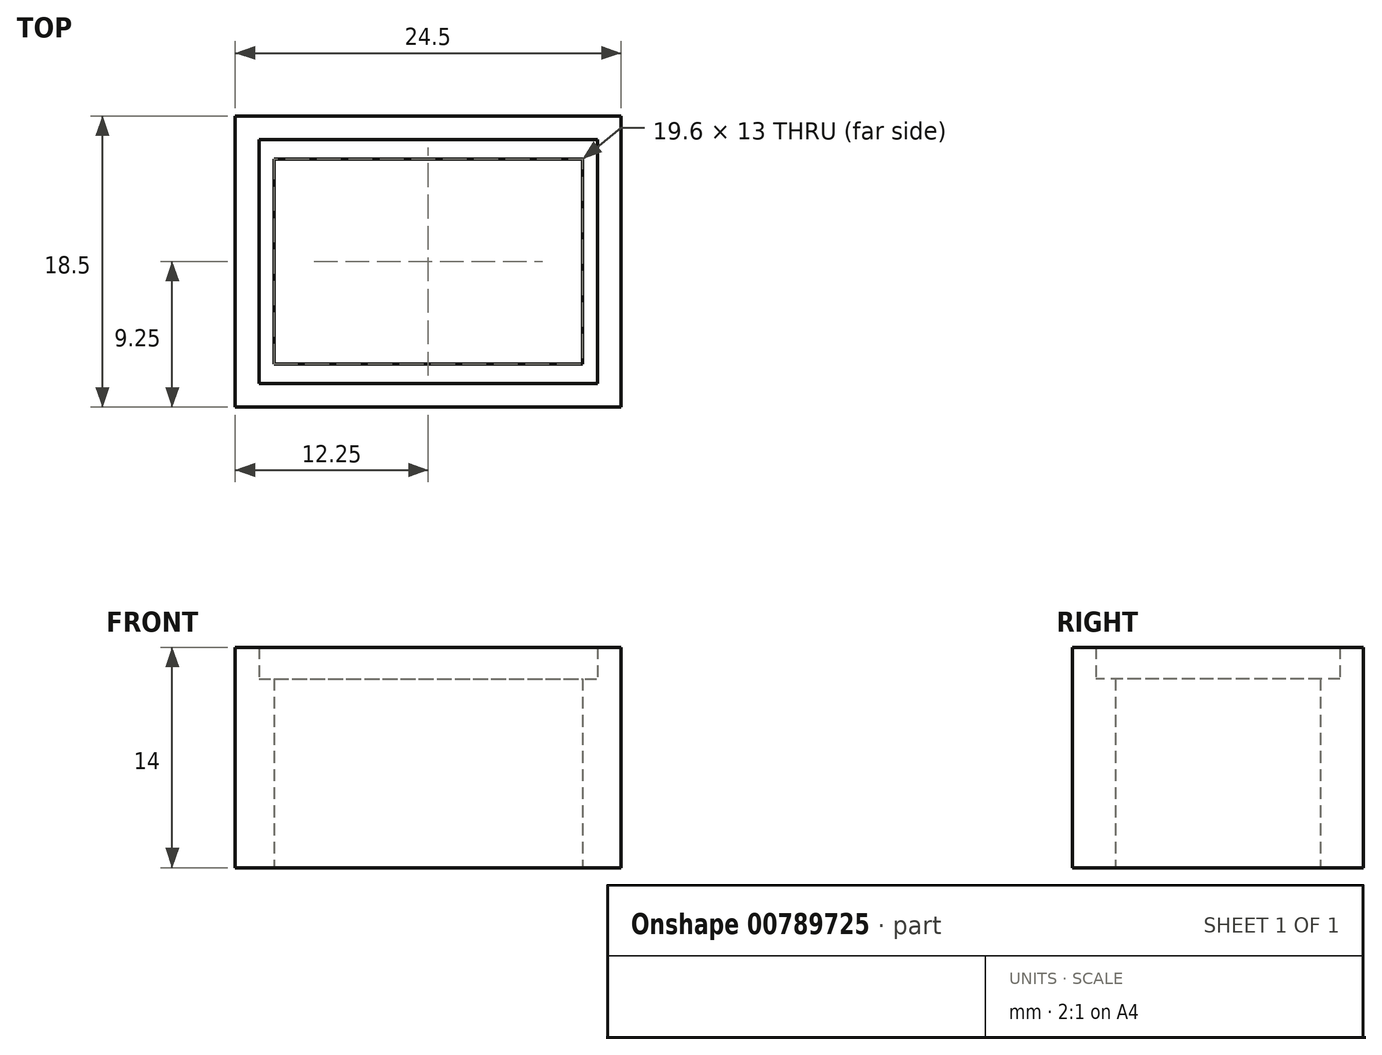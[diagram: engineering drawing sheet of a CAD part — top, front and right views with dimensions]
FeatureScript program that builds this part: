
annotation { "Feature Type Name" : "Feature", "Feature Type Description" : "" }
export const myFeature = defineFeature(function(context is Context, id is Id, definition is map)
    precondition{}
    {
        {
            var Q0;
            Q0=qCreatedBy(makeId("Top.planeOp"),FACE);
            var sketch = newSketch(context, id + "F0", { "sketchPlane" : qUnion([Q0])});
            skLineSegment(sketch, "E0.bottom", {"start": v(-9.8, 6.5) * mm, "end": v(9.8, 6.5) * mm});
            skLineSegment(sketch, "E0.top", {"start": v(-9.8, -6.5) * mm, "end": v(9.8, -6.5) * mm});
            skLineSegment(sketch, "E0.left", {"start": v(-9.8, 6.5) * mm, "end": v(-9.8, -6.5) * mm});
            skLineSegment(sketch, "E0.right", {"start": v(9.8, 6.5) * mm, "end": v(9.8, -6.5) * mm});
            skLineSegment(sketch, "E1.bottom", {"start": v(-10.75, 7.75) * mm, "end": v(10.75, 7.75) * mm});
            skLineSegment(sketch, "E1.top", {"start": v(-10.75, -7.75) * mm, "end": v(10.75, -7.75) * mm});
            skLineSegment(sketch, "E1.left", {"start": v(-10.75, 7.75) * mm, "end": v(-10.75, -7.75) * mm});
            skLineSegment(sketch, "E1.right", {"start": v(10.75, 7.75) * mm, "end": v(10.75, -7.75) * mm});
            skLineSegment(sketch, "E2.bottom", {"start": v(12.25, 9.25) * mm, "end": v(-12.25, 9.25) * mm});
            skLineSegment(sketch, "E2.top", {"start": v(12.25, -9.25) * mm, "end": v(-12.25, -9.25) * mm});
            skLineSegment(sketch, "E2.left", {"start": v(12.25, 9.25) * mm, "end": v(12.25, -9.25) * mm});
            skLineSegment(sketch, "E2.right", {"start": v(-12.25, 9.25) * mm, "end": v(-12.25, -9.25) * mm});
            skPoint(sketch, "E2.middle", {"position": v(0, 0) * mm});
            skSolve(sketch);
        }
        {
            var Q0;
            Q0=makeQuery(id+"F0.imprint","IMPRINT",FACE,{"disambiguationData":[TD([[makeQuery(id+"F0.imprint","IMPRINT",EDGE,{"derivedFrom":sQuery(id+"F0.wireOp",EDGE,"E0.bottom")}),1.0]])]});
            extrude(context, id + "F1", {"entities" : qUnion([Q0]), "depth" : 12 * mm, "offsetDistance" : 25 * mm});
        }
        {
            var Q0;
            Q0 = qSketchRegion(id + "F0", true);
            extrude(context, id + "F2", {"entities" : qUnion([Q0]), "operationType" : NewBodyOperationType.ADD, "depth" : 14 * mm, "offsetDistance" : 25 * mm});
        }
    });
